# Revit family: LTC-4RDW-P
name_source: partatom
category: Lighting Fixtures
units: mm (PartAtom-declared; Revit-internal decimal feet)

## family parameters
Cut with Voids When Loaded = No
Host = Face
Light Source = Yes
OmniClass Number = 23.80.70.11.14.11
OmniClass Title = Downlights
Part Type = Normal
Room Calculation Point = No
Round Connector Dimension = Use Diameter
Shared = No

## types (1)
- LTC-4RDW-P
    Apparent Load = 25 VA
    Ballast = Paint -  Carbon Black
    Certifications = • cCSAus certified to UL 1598
• Wall Mount: Suitable for wet locations
• Surface & Pendant Mount: Suitable for wet
locations under covered ceiling
• Cord Mount and all Wall Wash: Suitable for
damp locations
    Color Filter = 16777215
    Cord Height = 17.5 "
    Default Elevation = 48 "
    Description = LITEISTRY™ 4inch Round Cylinder
    Dimming Lamp Color Temperature Shift = <None>
    Emit Shape Visible in Rendering = No
    Emit from Circle Diameter = 5.6 "
    Features = •	4inch architectural LED round downlight and wall wash cylinder delivering 600 - 4000 lm
•	4 beam distributions from 0.4 to 1.2 Spacing Criteria
•	Quiet reflector appearance with 50º optical cutoff
•	2700K - 5000K, 80+ and 90+ CRI options
•	Available in Surface, Wall, Pendant, or Cord Mount configurations
•	Variety of dimming protocol options including 0-10V, DALI, DMX, Forward Phase and EcoSystem
•	NX Distributed Intelligence™ wired and wireless controls capability available
•	2 SDCM color consistency
•	Long life L90 at 55,000 hrs (TM-21)
•	Five year warranty
    Lamp = LED Lamp
    Manufacturer = Litecontrol
    Model = LTC-4RDW
    Photometric Web File = LTC-4RD-P-20L35K8MD-DM1-S-BL.ies
    Reflector = Glass - Glass
    Tilt Angle = -90.00°
    URL = https://www.currentlighting.com
    Voltage = 120 V
    Warranty = • 5 year warranty
• See HLI Standard Warranty for
additional information
    Wattage Comments = 8-52W

## geometry (parser evidence)
native form markers: Blend x2, Sweep x3
no freeform markers — native parametric forms only
